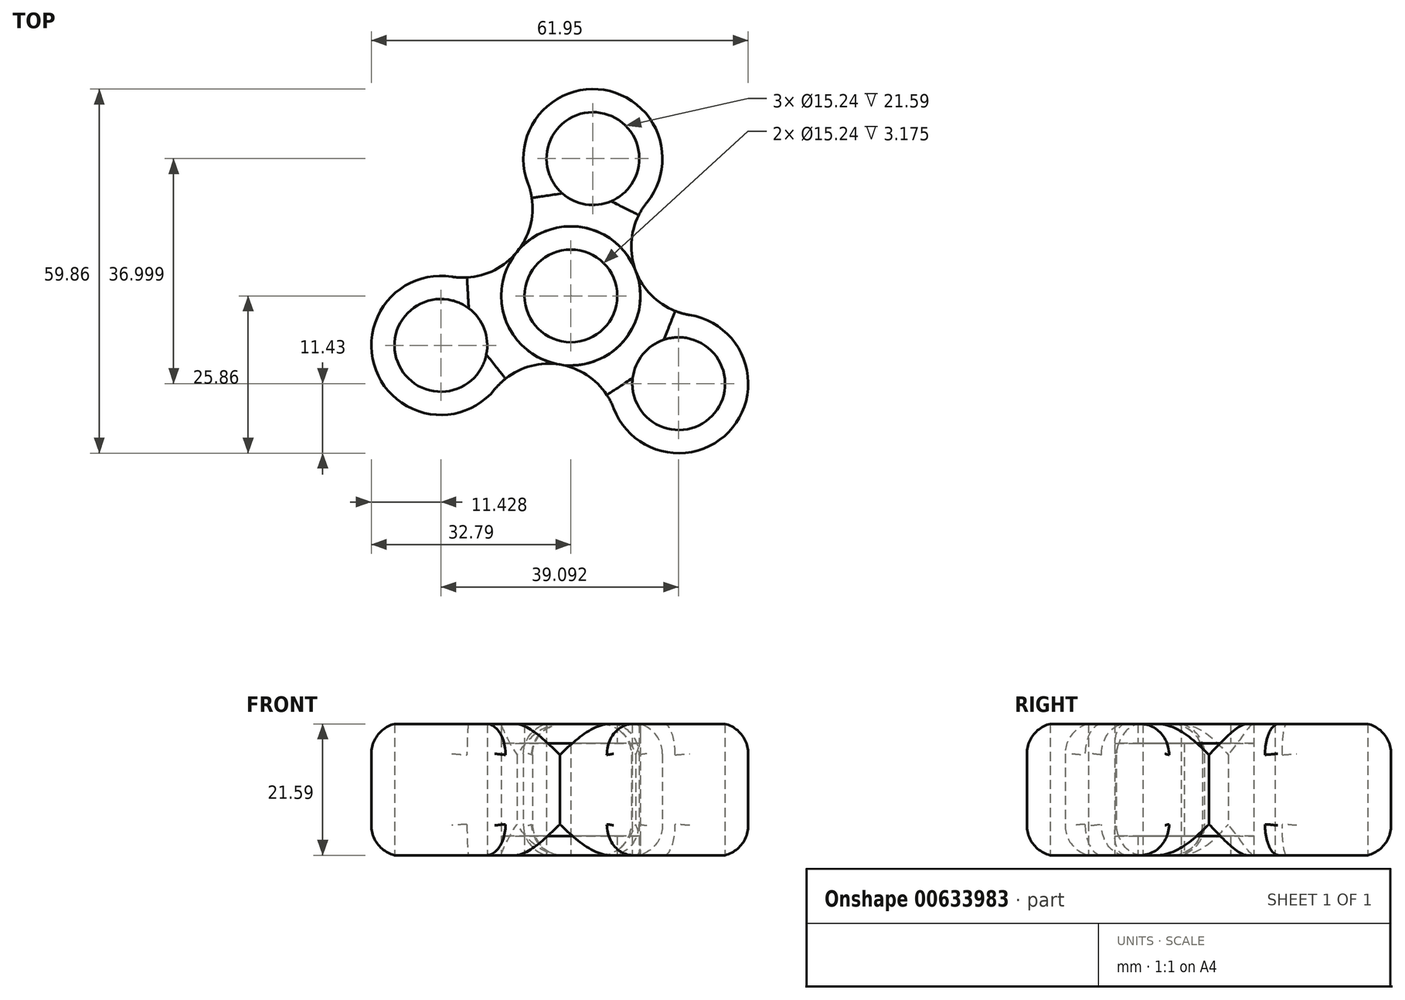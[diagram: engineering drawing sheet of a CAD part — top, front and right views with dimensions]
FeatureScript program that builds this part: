
annotation { "Feature Type Name" : "Feature", "Feature Type Description" : "" }
export const myFeature = defineFeature(function(context is Context, id is Id, definition is map)
    precondition{}
    {
        {
            var Q0;
            Q0=qCreatedBy(makeId("Top.planeOp"),FACE);
            var sketch = newSketch(context, id + "F0", { "sketchPlane" : qUnion([Q0])});
            skCircle(sketch, "E0", {"center": v(0, 0) * mm, "radius": 11.43 * mm});
            skArc(sketch, "E1", {"start": v(12.5, 15.35) * mm, "mid": v(10.68, 4.07) * mm, "end": v(19.55, -3.14) * mm});
            skArc(sketch, "E2", {"start": v(-19.55, 3.14) * mm, "mid": v(-8.87, 7.21) * mm, "end": v(-7.05, 18.5) * mm});
            skArc(sketch, "E3", {"start": v(7.05, -18.5) * mm, "mid": v(-1.82, -11.28) * mm, "end": v(-12.5, -15.35) * mm});
            skArc(sketch, "E4", {"start": v(12.5, 15.35) * mm, "mid": v(5.45, 33.85) * mm, "end": v(-7.05, 18.5) * mm});
            skArc(sketch, "E5", {"start": v(-19.55, 3.14) * mm, "mid": v(-32.04, -12.2) * mm, "end": v(-12.5, -15.35) * mm});
            skArc(sketch, "E6", {"start": v(7.05, -18.5) * mm, "mid": v(26.6, -21.64) * mm, "end": v(19.55, -3.14) * mm});
            skCircle(sketch, "E7", {"center": v(-21.36, -8.14) * mm, "radius": 7.62 * mm});
            skCircle(sketch, "E8", {"center": v(3.63, 22.57) * mm, "radius": 7.62 * mm});
            skCircle(sketch, "E9", {"center": v(17.73, -14.43) * mm, "radius": 7.62 * mm});
            skSolve(sketch);
        }
        {
            var Q0;
            {var subQ0=sQuery(id+"F0.wireOp",EDGE,"E5");Q0=makeQuery(id+"F0.imprint","IMPRINT",FACE,{"disambiguationData":[TD([[makeQuery(id+"F0.imprint","IMPRINT",EDGE,{"derivedFrom":subQ0}),1.0]])]});}
            var Q1;
            {var subQ0=sQuery(id+"F0.wireOp",EDGE,"E6");Q1=makeQuery(id+"F0.imprint","IMPRINT",FACE,{"disambiguationData":[TD([[makeQuery(id+"F0.imprint","IMPRINT",EDGE,{"derivedFrom":subQ0}),1.0]])]});}
            var Q2;
            {var subQ0=sQuery(id+"F0.wireOp",EDGE,"E4");Q2=makeQuery(id+"F0.imprint","IMPRINT",FACE,{"disambiguationData":[TD([[makeQuery(id+"F0.imprint","IMPRINT",EDGE,{"derivedFrom":subQ0}),1.0]])]});}
            extrude(context, id + "F1", {"entities" : qUnion([Q0, Q1, Q2]), "depth" : 21.59 * mm, "offsetDistance" : 25.4 * mm});
        }
        {
            var Q0;
            Q0=qCreatedBy(makeId("Top.planeOp"),FACE);
            var sketch = newSketch(context, id + "F2", { "sketchPlane" : qUnion([Q0])});
            skCircle(sketch, "E10", {"center": v(0, 0) * mm, "radius": 11.43 * mm});
            skCircle(sketch, "E11", {"center": v(0, 0) * mm, "radius": 7.62 * mm});
            skSolve(sketch);
        }
        {
            var Q0;
            Q0=makeQuery(id+"F2.imprint","IMPRINT",FACE,{"disambiguationData":[TD([[makeQuery(id+"F2.imprint","IMPRINT",EDGE,{"derivedFrom":sQuery(id+"F2.wireOp",EDGE,"E10")}),1.0]])]});
            extrude(context, id + "F3", {"entities" : qUnion([Q0]), "depth" : 3.17 * mm, "offsetDistance" : 25.4 * mm});
        }
        {
            var Q0;
            Q0=makeQuery(id+"F3.opExtrude","CAP_FACE",FACE,{"disambiguationData":[OSD([sQuery(id+"F2.wireOp",EDGE,"E10"),sQuery(id+"F2.wireOp",EDGE,"E11")])],"isStart":false});
            var sketch = newSketch(context, id + "F4", { "sketchPlane" : qUnion([Q0])});
            skCircle(sketch, "E12", {"center": v(0, 0) * mm, "radius": 11.03 * mm});
            skCircle(sketch, "E13", {"center": v(0, 0) * mm, "radius": 11.02 * mm});
            skCircle(sketch, "E14", {"center": v(0, 0) * mm, "radius": 10.9 * mm});
            skSolve(sketch);
        }
        {
            var Q0;
            Q0=sQuery(id+"F4.wireOp",EDGE,"E12");
            extrude(context, id + "F5", {"bodyType" : ToolBodyType.SURFACE, "surfaceEntities" : qUnion([Q0]), "depth" : 15.24 * mm, "offsetDistance" : 25.4 * mm});
        }
        {
            var Q0;
            Q0=qCreatedBy(makeId("Top.planeOp"),FACE);
            var sketch = newSketch(context, id + "F6", { "sketchPlane" : qUnion([Q0])});
            skCircle(sketch, "E15", {"center": v(0, 0) * mm, "radius": 0.01 * mm});
            skSolve(sketch);
        }
        {
            var Q0;
            Q0=makeQuery(id+"F6.imprint","IMPRINT",FACE,{"disambiguationData":[TD([[makeQuery(id+"F6.imprint","IMPRINT",EDGE,{"derivedFrom":sQuery(id+"F6.wireOp",EDGE,"E15")}),1.0]])]});
            extrude(context, id + "F7", {"entities" : qUnion([Q0]), "depth" : 18.41 * mm, "offsetDistance" : 25.4 * mm});
        }
        {
            var Q0;
            Q0=makeQuery(id+"F7.opExtrude","CAP_FACE",FACE,{"disambiguationData":[OSD([sQuery(id+"F6.wireOp",EDGE,"E15")])],"isStart":false});
            var sketch = newSketch(context, id + "F8", { "sketchPlane" : qUnion([Q0])});
            skCircle(sketch, "E16", {"center": v(0, 0) * mm, "radius": 11.43 * mm});
            skCircle(sketch, "E17", {"center": v(0, 0) * mm, "radius": 7.62 * mm});
            skSolve(sketch);
        }
        {
            var Q0;
            Q0=makeQuery(id+"F8.imprint","IMPRINT",FACE,{"disambiguationData":[TD([[makeQuery(id+"F8.imprint","IMPRINT",EDGE,{"derivedFrom":sQuery(id+"F8.wireOp",EDGE,"E16")}),1.0]])]});
            extrude(context, id + "F9", {"entities" : qUnion([Q0]), "depth" : 3.17 * mm, "offsetDistance" : 25.4 * mm});
        }
        {
            var Q0;
            {var subQ0=sQuery(id+"F0.wireOp",EDGE,"E3");Q0=makeQuery(id+"F1.opExtrude","CAP_EDGE",EDGE,{"disambiguationData":[OSD([subQ0]),TDD([makeQuery(id+"F0.imprint","IMPRINT",EDGE,{"disambiguationData":[TD([[makeQuery(id+"F0.imprint","INTERSECT",VERTEX,{"derivedFrom":[subQ0,sQuery(id+"F0.wireOp",EDGE,"E5")]}),1.0]])],"derivedFrom":subQ0})])],"isStart":false});}
            var Q1;
            Q1=makeQuery(id+"F1.opExtrude","CAP_EDGE",EDGE,{"disambiguationData":[OSD([sQuery(id+"F0.wireOp",EDGE,"E5")])],"isStart":false});
            var Q2;
            Q2=makeQuery(id+"F1.opExtrude","CAP_EDGE",EDGE,{"disambiguationData":[OSD([sQuery(id+"F0.wireOp",EDGE,"E6")])],"isStart":false});
            var Q3;
            {var subQ0=sQuery(id+"F0.wireOp",EDGE,"E1");Q3=makeQuery(id+"F1.opExtrude","CAP_EDGE",EDGE,{"disambiguationData":[OSD([subQ0]),TDD([makeQuery(id+"F0.imprint","IMPRINT",EDGE,{"disambiguationData":[TD([[makeQuery(id+"F0.imprint","INTERSECT",VERTEX,{"derivedFrom":[subQ0,sQuery(id+"F0.wireOp",EDGE,"E4")]}),-1.0]])],"derivedFrom":subQ0})])],"isStart":false});}
            var Q4;
            Q4=makeQuery(id+"F1.opExtrude","CAP_EDGE",EDGE,{"disambiguationData":[OSD([sQuery(id+"F0.wireOp",EDGE,"E6")])],"isStart":true});
            var Q5;
            {var subQ0=sQuery(id+"F0.wireOp",EDGE,"E3");Q5=makeQuery(id+"F1.opExtrude","CAP_EDGE",EDGE,{"disambiguationData":[OSD([subQ0]),TDD([makeQuery(id+"F0.imprint","IMPRINT",EDGE,{"disambiguationData":[TD([[makeQuery(id+"F0.imprint","INTERSECT",VERTEX,{"derivedFrom":[subQ0,sQuery(id+"F0.wireOp",EDGE,"E6")]}),-1.0]])],"derivedFrom":subQ0})])],"isStart":true});}
            var Q6;
            Q6=makeQuery(id+"F1.opExtrude","CAP_EDGE",EDGE,{"disambiguationData":[OSD([sQuery(id+"F0.wireOp",EDGE,"E5")])],"isStart":true});
            var Q7;
            {var subQ0=sQuery(id+"F0.wireOp",EDGE,"E2");Q7=makeQuery(id+"F1.opExtrude","CAP_EDGE",EDGE,{"disambiguationData":[OSD([subQ0]),TDD([makeQuery(id+"F0.imprint","IMPRINT",EDGE,{"disambiguationData":[TD([[makeQuery(id+"F0.imprint","INTERSECT",VERTEX,{"derivedFrom":[subQ0,sQuery(id+"F0.wireOp",EDGE,"E4")]}),1.0]])],"derivedFrom":subQ0})])],"isStart":true});}
            var Q8;
            Q8=makeQuery(id+"F1.opExtrude","CAP_EDGE",EDGE,{"disambiguationData":[OSD([sQuery(id+"F0.wireOp",EDGE,"E4")])],"isStart":true});
            fillet(context, id + "F10", {"entities" : qUnion([Q0, Q1, Q2, Q3, Q4, Q5, Q6, Q7, Q8]), "radius" : 5.08 * mm, "tangentPropagation" : true, "allowEdgeOverflow" : false});
        }
    });
